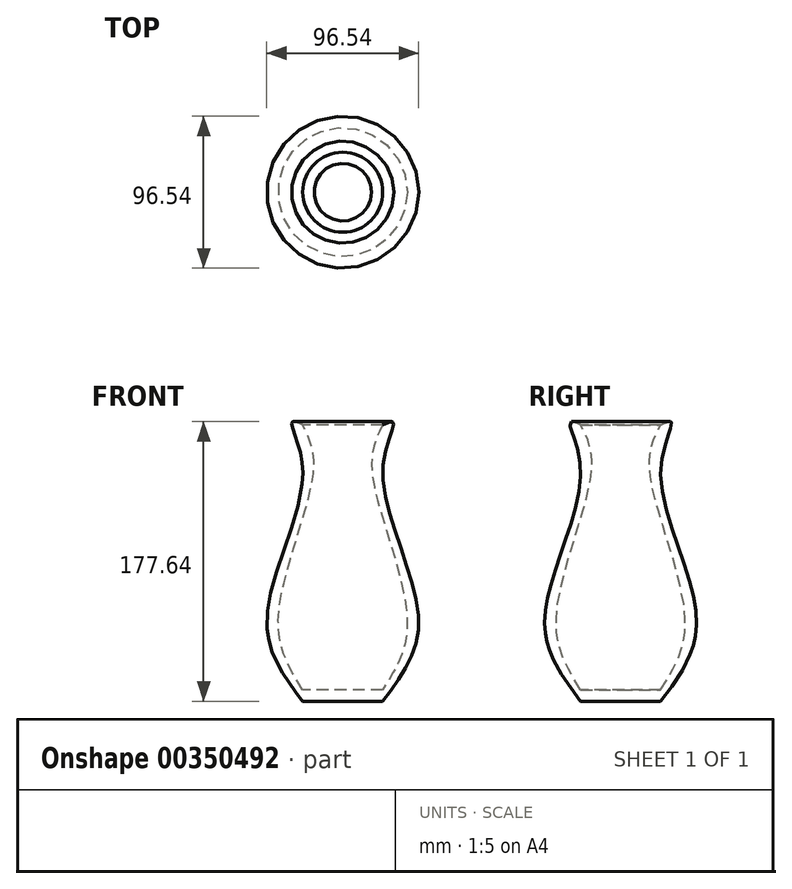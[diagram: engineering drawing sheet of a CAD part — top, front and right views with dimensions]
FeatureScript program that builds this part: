
annotation { "Feature Type Name" : "Feature", "Feature Type Description" : "" }
export const myFeature = defineFeature(function(context is Context, id is Id, definition is map)
    precondition{}
    {
        {
            var Q0;
            Q0=qCreatedBy(makeId("Right.planeOp"),FACE);
            var sketch = newSketch(context, id + "F0", { "sketchPlane" : qUnion([Q0])});
            skLineSegment(sketch, "E0", {"start": v(25.4, 0) * mm, "end": v(50.8, 0) * mm});
            skFitSpline(sketch, "E1", {"points": [v(50.8, 0) * mm, v(73.63, 52.63) * mm, v(50.8, 146.26) * mm, v(57.55, 177.28) * mm, v(50.8, 175.68) * mm], "startDerivative": vector(120.39, 158.22) * mm, "endDerivative": vector(-86.66, -38.21) * mm});
            skFitSpline(sketch, "E2", {"points": [v(50.8, 175.68) * mm, v(43.87, 146.22) * mm, v(66.33, 52.64) * mm, v(50.8, 7.33) * mm], "startDerivative": vector(-49.5, -96.73) * mm, "endDerivative": vector(-78.64, -123.56) * mm});
            skLineSegment(sketch, "E3", {"start": v(50.8, 7.33) * mm, "end": v(25.4, 7.33) * mm});
            skLineSegment(sketch, "E4", {"start": v(25.4, 7.33) * mm, "end": v(25.4, 0) * mm});
            skSolve(sketch);
        }
        {
            var Q0;
            Q0=makeQuery(id+"F0.imprint","IMPRINT",FACE,{"disambiguationData":[TD([[makeQuery(id+"F0.imprint","IMPRINT",EDGE,{"derivedFrom":sQuery(id+"F0.wireOp",EDGE,"E0")}),1.0]])]});
            var Q1;
            Q1=sQuery(id+"F0.wireOp",EDGE,"E4");
            revolve(context, id + "F1", {"entities" : qUnion([Q0]), "axis" : qUnion([Q1]), "revolveType" : RevolveType.FULL});
        }
    });
